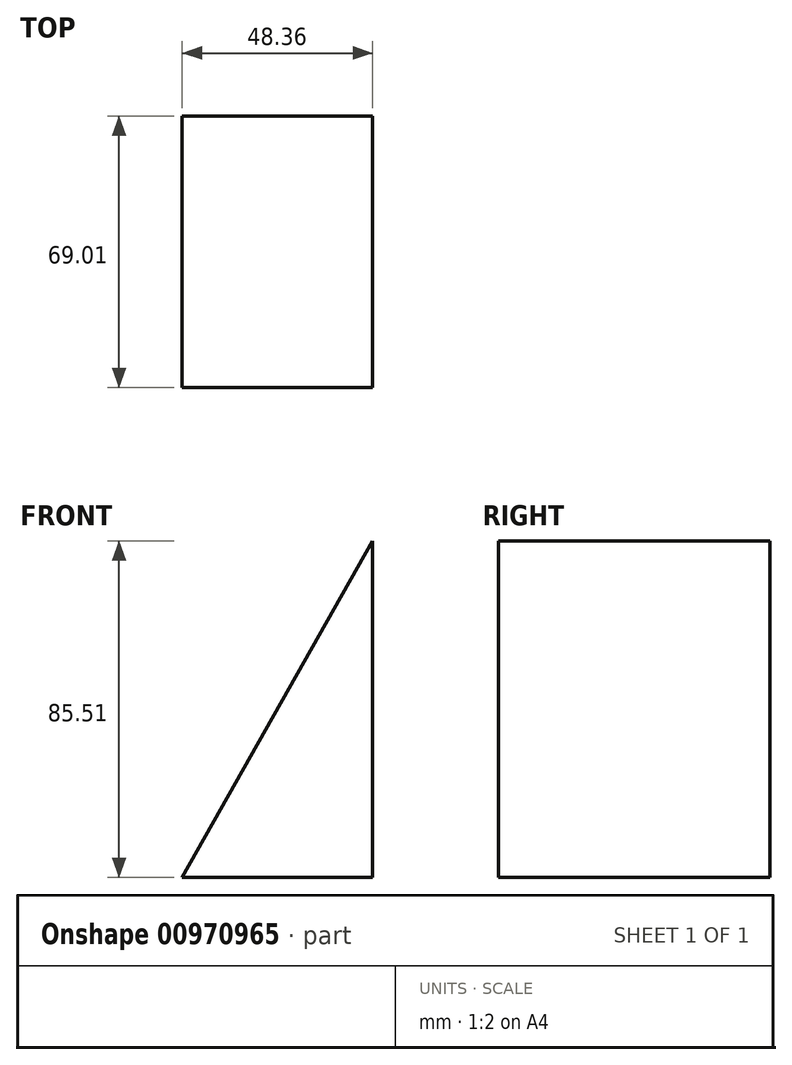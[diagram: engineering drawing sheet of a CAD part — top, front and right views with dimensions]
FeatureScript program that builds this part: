
annotation { "Feature Type Name" : "Feature", "Feature Type Description" : "" }
export const myFeature = defineFeature(function(context is Context, id is Id, definition is map)
    precondition{}
    {
        {
            var Q0;
            Q0=qCreatedBy(makeId("Front.planeOp"),FACE);
            var sketch = newSketch(context, id + "F0", { "sketchPlane" : qUnion([Q0])});
            skLineSegment(sketch, "E0", {"start": v(48.36, 85.5) * mm, "end": v(0, 0) * mm});
            skLineSegment(sketch, "E1", {"start": v(0, 0) * mm, "end": v(48.36, 0) * mm});
            skLineSegment(sketch, "E2", {"start": v(48.36, 0) * mm, "end": v(48.36, 85.5) * mm});
            skLineSegment(sketch, "E3", {"start": v(31.28, 66.66) * mm, "end": v(-31.53, 30.48) * mm});
            skLineSegment(sketch, "E4", {"start": v(-31.53, 30.48) * mm, "end": v(0, 0) * mm});
            skLineSegment(sketch, "E5", {"start": v(0, 0) * mm, "end": v(31.28, 66.66) * mm});
            skSolve(sketch);
        }
        {
            var Q0;
            Q0=makeQuery(id+"F0.imprint","IMPRINT",FACE,{"disambiguationData":[TD([[makeQuery(id+"F0.imprint","IMPRINT",EDGE,{"derivedFrom":sQuery(id+"F0.wireOp",EDGE,"E0")}),1.0]])]});
            extrude(context, id + "F1", {"entities" : qUnion([Q0]), "depth" : 69 * mm, "offsetDistance" : 25.4 * mm});
        }
    });
